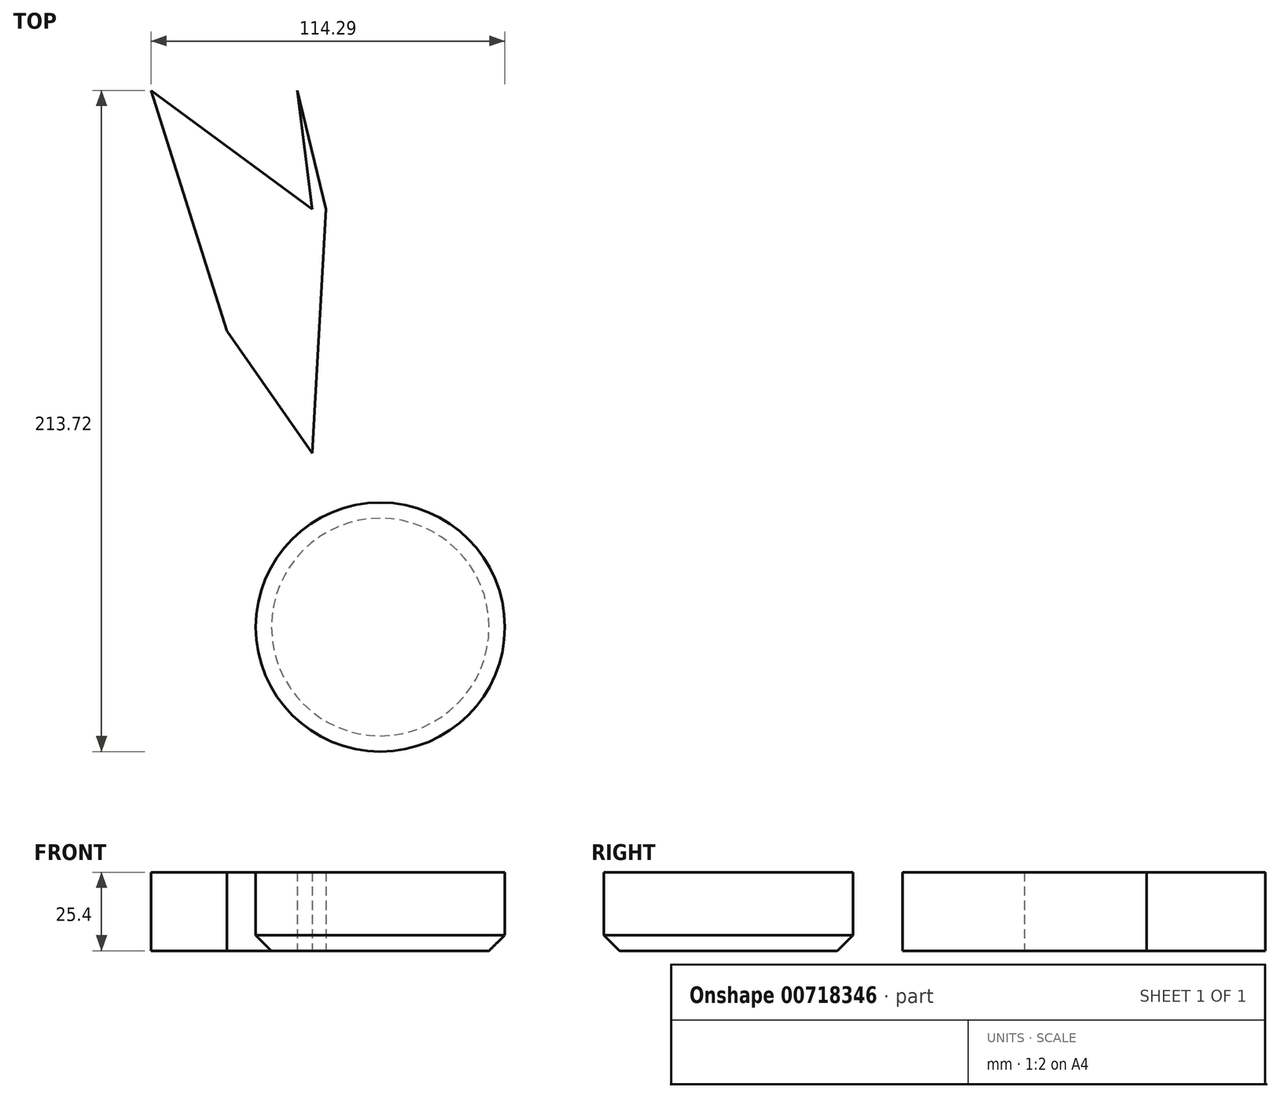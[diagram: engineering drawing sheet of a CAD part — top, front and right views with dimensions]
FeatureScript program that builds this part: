
annotation { "Feature Type Name" : "Feature", "Feature Type Description" : "" }
export const myFeature = defineFeature(function(context is Context, id is Id, definition is map)
    precondition{}
    {
        {
            var Q0;
            Q0=qCreatedBy(makeId("Top.planeOp"),FACE);
            var sketch = newSketch(context, id + "F0", { "sketchPlane" : qUnion([Q0])});
            skLineSegment(sketch, "E0", {"start": v(-88.4, 41.4) * mm, "end": v(-65.4, 0) * mm});
            skLineSegment(sketch, "E1", {"start": v(103.95, 84.56) * mm, "end": v(131.45, 45.08) * mm});
            skLineSegment(sketch, "E2", {"start": v(131.45, 45.08) * mm, "end": v(121.76, 91.71) * mm});
            skLineSegment(sketch, "E3", {"start": v(121.76, 91.71) * mm, "end": v(103.95, 84.56) * mm});
            skLineSegment(sketch, "E4", {"start": v(103.95, 84.56) * mm, "end": v(79.42, 162.33) * mm});
            skLineSegment(sketch, "E5", {"start": v(79.42, 162.33) * mm, "end": v(121.76, 91.71) * mm});
            skLineSegment(sketch, "E6", {"start": v(121.76, 91.71) * mm, "end": v(131.45, 123.96) * mm});
            skLineSegment(sketch, "E7", {"start": v(131.45, 123.96) * mm, "end": v(79.42, 162.33) * mm});
            skLineSegment(sketch, "E8", {"start": v(135.95, 123.96) * mm, "end": v(131.45, 45.08) * mm});
            skLineSegment(sketch, "E9", {"start": v(135.95, 123.96) * mm, "end": v(126.6, 162.33) * mm});
            skPoint(sketch, "E9.endSnap0", {"position": v(126.6, 107.84) * mm});
            skLineSegment(sketch, "E10", {"start": v(126.6, 162.33) * mm, "end": v(131.45, 123.96) * mm});
            skCircle(sketch, "E11", {"center": v(153.47, -11.15) * mm, "radius": 40.24 * mm});
            skArc(sketch, "E12", {"start": v(172.65, 24.22) * mm, "mid": v(203.85, 32.28) * mm, "end": v(180.72, 54.72) * mm});
            skArc(sketch, "E13", {"start": v(157.46, -51.2) * mm, "mid": v(125.31, -63.81) * mm, "end": v(154.13, -82.85) * mm});
            skArc(sketch, "E14", {"start": v(114.8, 0) * mm, "mid": v(122.58, 27.99) * mm, "end": v(95.74, 39.08) * mm});
            skArc(sketch, "E15", {"start": v(191.55, -71.7) * mm, "mid": v(207.06, -49.88) * mm, "end": v(182.7, -38.81) * mm});
            skSolve(sketch);
        }
        {
            var Q0;
            Q0 = qSketchRegion(id + "F0", true);
            extrude(context, id + "F1", {"entities" : qUnion([Q0]), "depth" : 25.4 * mm, "offsetDistance" : 25.4 * mm});
        }
        {
            var Q0;
            Q0=makeQuery(id+"F1.opExtrude","CAP_FACE",FACE,{"disambiguationData":[OSD([sQuery(id+"F0.wireOp",EDGE,"E11")])],"isStart":true});
            chamfer(context, id + "F2", {"entities" : qUnion([Q0]), "width" : 5.08 * mm, "tangentPropagation" : true});
        }
    });
